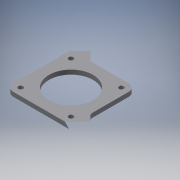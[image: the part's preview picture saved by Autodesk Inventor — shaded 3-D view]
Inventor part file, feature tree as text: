
AUTODESK INVENTOR PART (.ipt)
format: ipt  version: 2016 (Build 200138000, 138)  size: 147,456 bytes
history: native  units: mm
features: extrude x4, sketch x4, reference x4, fillet x1
ambient origin geometry x8: Origin, YZ Plane, XZ Plane, XY Plane, X Axis, Y Axis, Z Axis, Center Point
bodies: Solid1 (feature_tree)
feature tree (13):
  extrude  "Extrusion1"  Depth=90.0mm
  extrude  "Extrusion2"  Depth=6.0mm TaperAngle=0.0deg
  extrude  "Extrusion3"  Depth=6.0mm TaperAngle=0.0deg
  fillet  "Fillet1"  Radius=6.0mm
  extrude  "Extrusion4"  Depth=7.0mm
  sketch  "Sketch1"  dims[d0=90.0mm d1=90.0mm]
  sketch  "Sketch2"  dims[d2=10.0mm d3=6.0mm d4=0.0mm]
  sketch  "Sketch3"  dims[d5=61.0mm d6=6.0mm d7=0.0mm d9=6.0mm d10=0.0mm]
  sketch  "Sketch4"  dims[d13=53.5mm d15=7.0mm d16=10.0mm d17=0.0mm]
  reference  "Reference1"
  reference  "Reference2"
  reference  "Reference3"
  reference  "Reference4"
